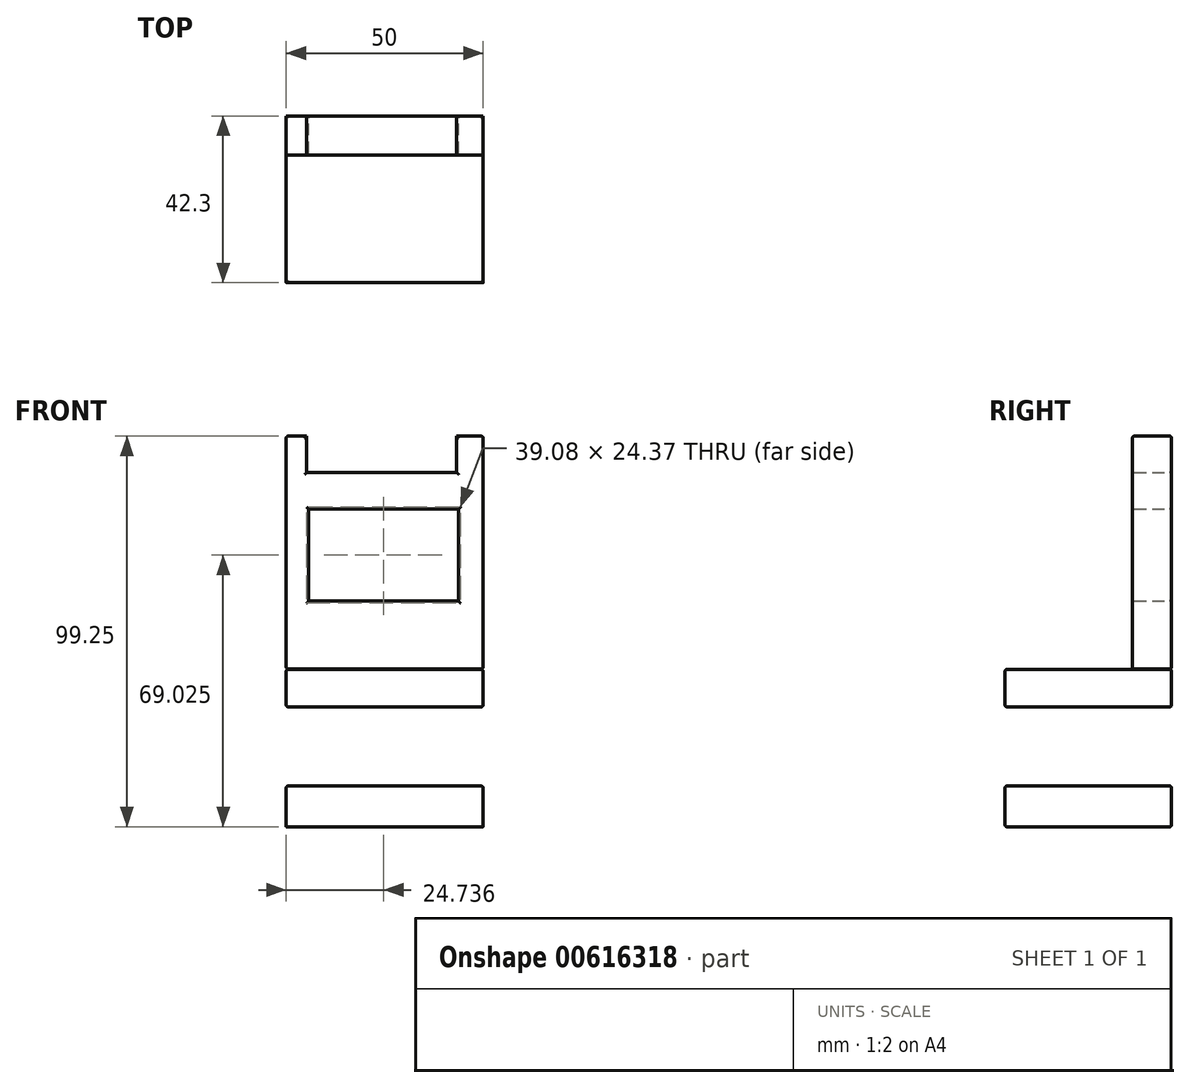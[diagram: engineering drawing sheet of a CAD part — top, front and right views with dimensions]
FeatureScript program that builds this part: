
annotation { "Feature Type Name" : "Feature", "Feature Type Description" : "" }
export const myFeature = defineFeature(function(context is Context, id is Id, definition is map)
    precondition{}
    {
        {
            var Q0;
            Q0=qCreatedBy(makeId("Right.planeOp"),FACE);
            var sketch = newSketch(context, id + "F0", { "sketchPlane" : qUnion([Q0])});
            skLineSegment(sketch, "E0.bottom", {"start": v(-9.94, 68.8) * mm, "end": v(0, 68.8) * mm});
            skLineSegment(sketch, "E0.top", {"start": v(-9.94, 9.7) * mm, "end": v(0, 9.7) * mm});
            skLineSegment(sketch, "E0.left", {"start": v(-9.94, 68.8) * mm, "end": v(-9.94, 9.7) * mm});
            skLineSegment(sketch, "E0.right", {"start": v(0, 68.8) * mm, "end": v(0, 9.7) * mm});
            skLineSegment(sketch, "E1.bottom", {"start": v(0, 0) * mm, "end": v(-42.3, 0) * mm});
            skLineSegment(sketch, "E1.top", {"start": v(0, 9.54) * mm, "end": v(-42.3, 9.54) * mm});
            skLineSegment(sketch, "E1.left", {"start": v(0, 0) * mm, "end": v(0, 9.54) * mm});
            skLineSegment(sketch, "E1.right", {"start": v(-42.3, 0) * mm, "end": v(-42.3, 9.54) * mm});
            skLineSegment(sketch, "E2.bottom", {"start": v(-42.3, 0) * mm, "end": v(-31.8, 0) * mm});
            skLineSegment(sketch, "E2.top", {"start": v(-42.3, -20.1) * mm, "end": v(-31.8, -20.1) * mm});
            skLineSegment(sketch, "E2.right", {"start": v(-31.8, 0) * mm, "end": v(-31.8, -20.1) * mm});
            skLineSegment(sketch, "E3.bottom", {"start": v(-42.3, -20.1) * mm, "end": v(0, -20.1) * mm});
            skLineSegment(sketch, "E3.top", {"start": v(-42.3, -30.45) * mm, "end": v(0, -30.45) * mm});
            skLineSegment(sketch, "E3.left", {"start": v(-42.3, -20.1) * mm, "end": v(-42.3, -30.45) * mm});
            skLineSegment(sketch, "E3.right", {"start": v(0, -20.1) * mm, "end": v(0, -30.45) * mm});
            skLineSegment(sketch, "E4", {"start": v(-37.05, 0) * mm, "end": v(-37.05, -20.1) * mm});
            skSolve(sketch);
        }
        {
            var Q0;
            Q0=makeQuery(id+"F0.imprint","IMPRINT",FACE,{"disambiguationData":[TD([[makeQuery(id+"F0.imprint","IMPRINT",EDGE,{"derivedFrom":sQuery(id+"F0.wireOp",EDGE,"E0.bottom")}),-1.0]])]});
            var Q1;
            Q1=makeQuery(id+"F0.imprint","IMPRINT",FACE,{"disambiguationData":[TD([[makeQuery(id+"F0.imprint","IMPRINT",EDGE,{"derivedFrom":sQuery(id+"F0.wireOp",EDGE,"E1.bottom")}),-1.0]])]});
            var Q2;
            Q2=makeQuery(id+"F0.imprint","IMPRINT",FACE,{"disambiguationData":[TD([[makeQuery(id+"F0.imprint","IMPRINT",EDGE,{"derivedFrom":sQuery(id+"F0.wireOp",EDGE,"E2.bottom")}),-1.0]])]});
            var Q3;
            Q3=makeQuery(id+"F0.imprint","IMPRINT",FACE,{"disambiguationData":[TD([[makeQuery(id+"F0.imprint","IMPRINT",EDGE,{"derivedFrom":sQuery(id+"F0.wireOp",EDGE,"E3.top")}),1.0]])]});
            extrude(context, id + "F1", {"entities" : qUnion([Q0, Q1, Q2, Q3]), "depth" : 50 * mm, "offsetDistance" : 25 * mm});
        }
        {
            var Q0;
            Q0=qCreatedBy(makeId("Front.planeOp"),FACE);
            var sketch = newSketch(context, id + "F2", { "sketchPlane" : qUnion([Q0])});
            skLineSegment(sketch, "E5.bottom", {"start": v(5.7, 50.26) * mm, "end": v(43.78, 50.26) * mm});
            skLineSegment(sketch, "E5.top", {"start": v(5.7, 26.89) * mm, "end": v(43.78, 26.89) * mm});
            skLineSegment(sketch, "E5.left", {"start": v(5.7, 50.26) * mm, "end": v(5.7, 26.89) * mm});
            skLineSegment(sketch, "E5.right", {"start": v(43.78, 50.26) * mm, "end": v(43.78, 26.89) * mm});
            skLineSegment(sketch, "E6.bottom", {"start": v(5.22, 71.92) * mm, "end": v(43.26, 71.92) * mm});
            skLineSegment(sketch, "E6.top", {"start": v(5.22, 59.6) * mm, "end": v(43.26, 59.6) * mm});
            skLineSegment(sketch, "E6.left", {"start": v(5.22, 71.92) * mm, "end": v(5.22, 59.6) * mm});
            skLineSegment(sketch, "E6.right", {"start": v(43.26, 71.92) * mm, "end": v(43.26, 59.6) * mm});
            skSolve(sketch);
        }
        {
            var Q0;
            Q0=makeQuery(id+"F2.imprint","IMPRINT",FACE,{"disambiguationData":[TD([[makeQuery(id+"F2.imprint","IMPRINT",EDGE,{"derivedFrom":sQuery(id+"F2.wireOp",EDGE,"E5.bottom")}),-1.0]])]});
            var Q1;
            Q1=makeQuery(id+"F2.imprint","IMPRINT",FACE,{"disambiguationData":[TD([[makeQuery(id+"F2.imprint","IMPRINT",EDGE,{"derivedFrom":sQuery(id+"F2.wireOp",EDGE,"E6.bottom")}),-1.0]])]});
            extrude(context, id + "F3", {"entities" : qUnion([Q0, Q1]), "operationType" : NewBodyOperationType.REMOVE, "depth" : 25 * mm, "offsetDistance" : 25 * mm});
        }
        {
            var Q0;
            Q0=makeQuery(id+"F1.opExtrude","SWEPT_FACE",FACE,{"disambiguationData":[OSD([sQuery(id+"F0.wireOp",EDGE,"E1.top")])]});
            var Q1;
            Q1=makeQuery(id+"F1.opExtrude","SWEPT_FACE",FACE,{"disambiguationData":[OSD([sQuery(id+"F0.wireOp",EDGE,"E0.left")])]});
            var Q2;
            Q2=makeQuery(id+"F1.opExtrude","CAP_FACE",FACE,{"disambiguationData":[OSD([sQuery(id+"F0.wireOp",EDGE,"E0.bottom"),sQuery(id+"F0.wireOp",EDGE,"E0.top"),sQuery(id+"F0.wireOp",EDGE,"E0.left"),sQuery(id+"F0.wireOp",EDGE,"E0.right")])],"isStart":true});
            var Q3;
            Q3=makeQuery(id+"F1.opExtrude","CAP_FACE",FACE,{"disambiguationData":[OSD([sQuery(id+"F0.wireOp",EDGE,"E1.bottom"),sQuery(id+"F0.wireOp",EDGE,"E1.top"),sQuery(id+"F0.wireOp",EDGE,"E1.left"),sQuery(id+"F0.wireOp",EDGE,"E1.right"),sQuery(id+"F0.wireOp",EDGE,"E2.bottom"),sQuery(id+"F0.wireOp",EDGE,"E2.right"),sQuery(id+"F0.wireOp",EDGE,"E3.bottom"),sQuery(id+"F0.wireOp",EDGE,"E3.top"),sQuery(id+"F0.wireOp",EDGE,"E3.left"),sQuery(id+"F0.wireOp",EDGE,"E3.right"),sQuery(id+"F0.wireOp",EDGE,"E4")])],"isStart":true});
            var Q4;
            Q4=makeQuery(id+"F1.opExtrude","SWEPT_EDGE",EDGE,{"disambiguationData":[OSD([sQuery(id+"F0.wireOp",EDGE,"E1.right"),sQuery(id+"F0.wireOp",EDGE,"E2.bottom")])]});
            var Q5;
            Q5=makeQuery(id+"F1.opExtrude","SWEPT_FACE",FACE,{"disambiguationData":[OSD([sQuery(id+"F0.wireOp",EDGE,"E4")])]});
            var Q6;
            Q6=makeQuery(id+"F1.opExtrude","SWEPT_EDGE",EDGE,{"disambiguationData":[OSD([sQuery(id+"F0.wireOp",EDGE,"E3.top"),sQuery(id+"F0.wireOp",EDGE,"E3.left")])]});
            var Q7;
            Q7=makeQuery(id+"F1.opExtrude","CAP_FACE",FACE,{"disambiguationData":[OSD([sQuery(id+"F0.wireOp",EDGE,"E1.bottom"),sQuery(id+"F0.wireOp",EDGE,"E1.top"),sQuery(id+"F0.wireOp",EDGE,"E1.left"),sQuery(id+"F0.wireOp",EDGE,"E1.right"),sQuery(id+"F0.wireOp",EDGE,"E2.bottom"),sQuery(id+"F0.wireOp",EDGE,"E2.right"),sQuery(id+"F0.wireOp",EDGE,"E3.bottom"),sQuery(id+"F0.wireOp",EDGE,"E3.top"),sQuery(id+"F0.wireOp",EDGE,"E3.left"),sQuery(id+"F0.wireOp",EDGE,"E3.right"),sQuery(id+"F0.wireOp",EDGE,"E4")])],"isStart":false});
            var Q8;
            Q8=makeQuery(id+"F1.opExtrude","CAP_FACE",FACE,{"disambiguationData":[OSD([sQuery(id+"F0.wireOp",EDGE,"E0.bottom"),sQuery(id+"F0.wireOp",EDGE,"E0.top"),sQuery(id+"F0.wireOp",EDGE,"E0.left"),sQuery(id+"F0.wireOp",EDGE,"E0.right")])],"isStart":false});
            var Q9;
            Q9=makeQuery(id+"F1.opExtrude","SWEPT_FACE",FACE,{"disambiguationData":[OSD([sQuery(id+"F0.wireOp",EDGE,"E0.right")])]});
            var Q10;
            Q10=makeQuery(id+"F1.opExtrude","SWEPT_FACE",FACE,{"disambiguationData":[OSD([sQuery(id+"F0.wireOp",EDGE,"E1.left")])]});
            var Q11;
            Q11=makeQuery(id+"F1.opExtrude","SWEPT_FACE",FACE,{"disambiguationData":[OSD([sQuery(id+"F0.wireOp",EDGE,"E2.right")])]});
            var Q12;
            {var subQ0=sQuery(id+"F0.wireOp",EDGE,"E3.bottom");Q12=makeQuery(id+"F1.opExtrude","SWEPT_FACE",FACE,{"disambiguationData":[OSD([subQ0]),TDD([makeQuery(id+"F0.imprint","IMPRINT",EDGE,{"disambiguationData":[TD([[makeQuery(id+"F0.imprint","INTERSECT",VERTEX,{"derivedFrom":[sQuery(id+"F0.wireOp",EDGE,"E2.right"),subQ0]}),-1.0]])],"derivedFrom":subQ0})])]});}
            var Q13;
            Q13=makeQuery(id+"F1.opExtrude","SWEPT_EDGE",EDGE,{"disambiguationData":[OSD([sQuery(id+"F0.wireOp",EDGE,"E3.top"),sQuery(id+"F0.wireOp",EDGE,"E3.right")])]});
            fillet(context, id + "F4", {"entities" : qUnion([Q0, Q1, Q2, Q3, Q4, Q5, Q6, Q7, Q8, Q9, Q10, Q11, Q12, Q13]), "radius" : 0.5 * mm, "tangentPropagation" : true, "allowEdgeOverflow" : false});
        }
    });
